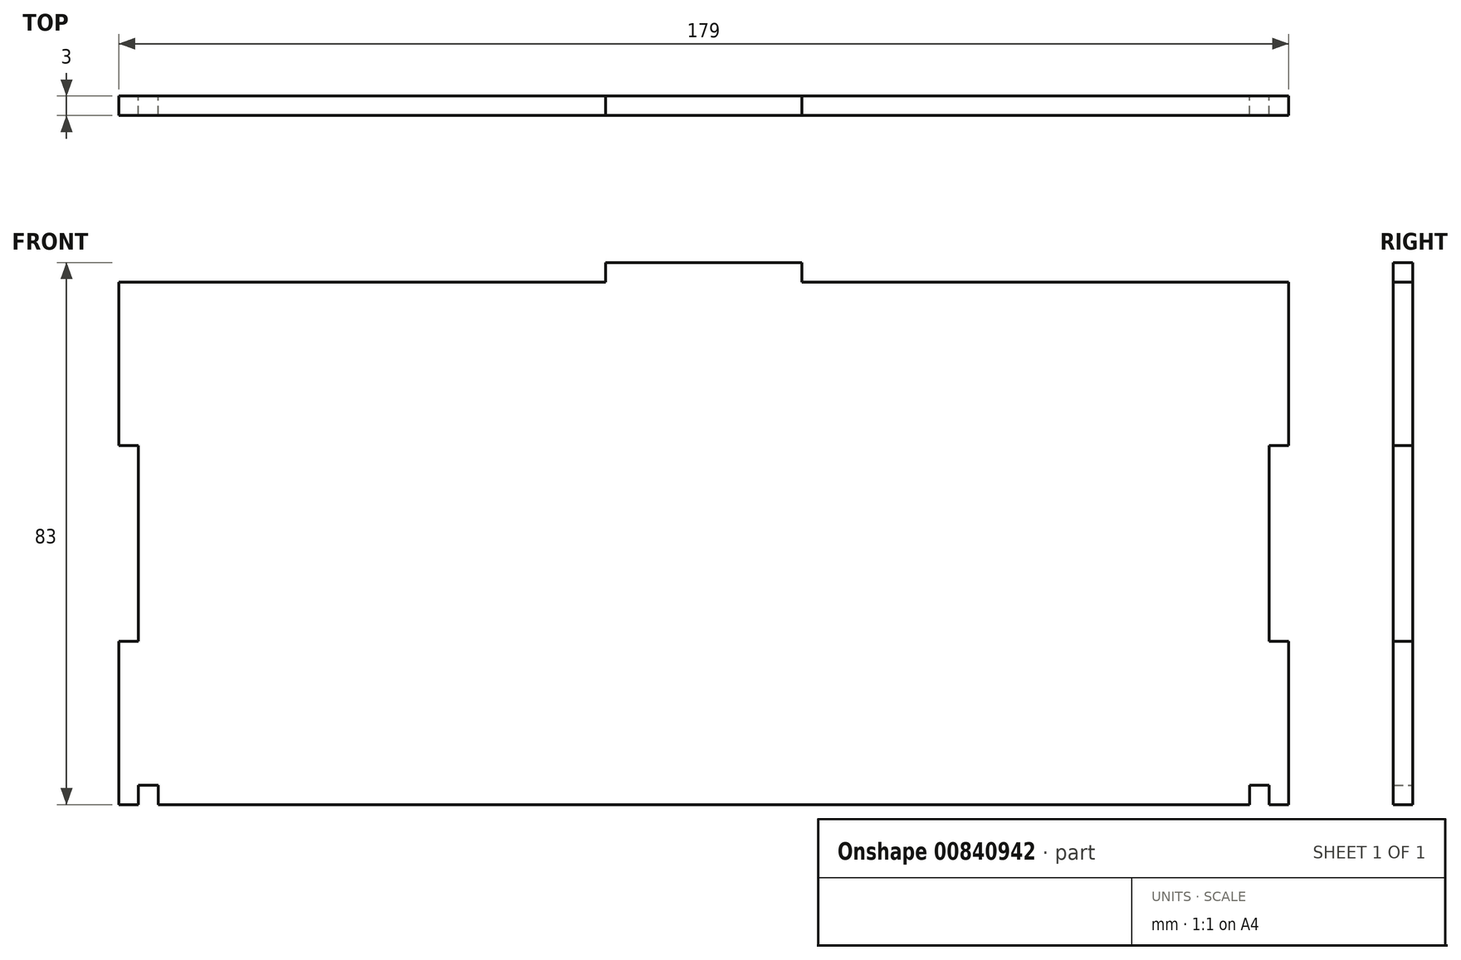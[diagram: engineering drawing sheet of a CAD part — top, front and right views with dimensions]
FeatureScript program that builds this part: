
annotation { "Feature Type Name" : "Feature", "Feature Type Description" : "" }
export const myFeature = defineFeature(function(context is Context, id is Id, definition is map)
    precondition{}
    {
        {
            var Q0;
            Q0=qCreatedBy(makeId("Front.planeOp"),FACE);
            var sketch = newSketch(context, id + "F0", { "sketchPlane" : qUnion([Q0])});
            skLineSegment(sketch, "E0.bottom", {"start": v(-83.25, 1.34) * mm, "end": v(95.75, 1.34) * mm});
            skLineSegment(sketch, "E0.top", {"start": v(-83.25, -78.66) * mm, "end": v(-80.25, -78.66) * mm});
            skLineSegment(sketch, "E0.left", {"start": v(-83.25, 1.34) * mm, "end": v(-83.25, -78.66) * mm});
            skLineSegment(sketch, "E0.right", {"start": v(95.75, 1.34) * mm, "end": v(95.75, -78.66) * mm});
            skLineSegment(sketch, "E1.top", {"start": v(-80.25, -75.66) * mm, "end": v(-77.25, -75.66) * mm});
            skLineSegment(sketch, "E1.left", {"start": v(-80.25, -78.66) * mm, "end": v(-80.25, -75.66) * mm});
            skLineSegment(sketch, "E1.right", {"start": v(-77.25, -78.66) * mm, "end": v(-77.25, -75.66) * mm});
            skLineSegment(sketch, "E2", {"start": v(6.25, 1.34) * mm, "end": v(6.25, -25.5) * mm, "construction": true});
            skLineSegment(sketch, "E3.trimOffspring", {"start": v(-77.25, -78.66) * mm, "end": v(89.75, -78.66) * mm});
            skLineSegment(sketch, "E4.MirrorCS", {"start": v(92.75, -78.66) * mm, "end": v(92.75, -75.66) * mm});
            skLineSegment(sketch, "E5.MirrorCS", {"start": v(92.75, -75.66) * mm, "end": v(89.75, -75.66) * mm});
            skLineSegment(sketch, "E6.MirrorCS", {"start": v(89.75, -78.66) * mm, "end": v(89.75, -75.66) * mm});
            skLineSegment(sketch, "E7.trimOffspring", {"start": v(92.75, -78.66) * mm, "end": v(95.75, -78.66) * mm});
            skLineSegment(sketch, "E8.bottom", {"start": v(-8.75, 4.34) * mm, "end": v(21.25, 4.34) * mm});
            skLineSegment(sketch, "E8.top", {"start": v(-8.75, 1.34) * mm, "end": v(21.25, 1.34) * mm});
            skLineSegment(sketch, "E8.left", {"start": v(-8.75, 4.34) * mm, "end": v(-8.75, 1.34) * mm});
            skLineSegment(sketch, "E8.right", {"start": v(21.25, 4.34) * mm, "end": v(21.25, 1.34) * mm});
            skSolve(sketch);
        }
        {
            var Q0;
            Q0 = qSketchRegion(id + "F0", true);
            extrude(context, id + "F1", {"entities" : qUnion([Q0]), "depth" : 3 * mm, "offsetDistance" : 25 * mm});
        }
        {
            var Q0;
            Q0=makeQuery(id+"F1.opExtrude","CAP_FACE",FACE,{"disambiguationData":[OSD([sQuery(id+"F0.wireOp",EDGE,"E0.bottom"),sQuery(id+"F0.wireOp",EDGE,"E0.top"),sQuery(id+"F0.wireOp",EDGE,"E0.left"),sQuery(id+"F0.wireOp",EDGE,"E0.right"),sQuery(id+"F0.wireOp",EDGE,"E1.top"),sQuery(id+"F0.wireOp",EDGE,"E1.left"),sQuery(id+"F0.wireOp",EDGE,"E1.right"),sQuery(id+"F0.wireOp",EDGE,"E3.trimOffspring"),sQuery(id+"F0.wireOp",EDGE,"E4.MirrorCS"),sQuery(id+"F0.wireOp",EDGE,"E5.MirrorCS"),sQuery(id+"F0.wireOp",EDGE,"E6.MirrorCS"),sQuery(id+"F0.wireOp",EDGE,"E7.trimOffspring")])],"isStart":false});
            var sketch = newSketch(context, id + "F2", { "sketchPlane" : qUnion([Q0])});
            skLineSegment(sketch, "E9.bottom", {"start": v(-83.25, -23.66) * mm, "end": v(-80.25, -23.66) * mm});
            skLineSegment(sketch, "E9.top", {"start": v(-83.25, -53.66) * mm, "end": v(-80.25, -53.66) * mm});
            skLineSegment(sketch, "E9.left", {"start": v(-83.25, -23.66) * mm, "end": v(-83.25, -53.66) * mm});
            skLineSegment(sketch, "E9.right", {"start": v(-80.25, -23.66) * mm, "end": v(-80.25, -53.66) * mm});
            skLineSegment(sketch, "E10", {"start": v(6.25, 4.34) * mm, "end": v(6.25, -35.76) * mm, "construction": true});
            skLineSegment(sketch, "E11.MirrorCS", {"start": v(95.75, -53.66) * mm, "end": v(92.75, -53.66) * mm});
            skLineSegment(sketch, "E12.MirrorCS", {"start": v(95.75, -23.66) * mm, "end": v(92.75, -23.66) * mm});
            skLineSegment(sketch, "E13.MirrorCS", {"start": v(92.75, -23.66) * mm, "end": v(92.75, -53.66) * mm});
            skLineSegment(sketch, "E14.MirrorCS", {"start": v(95.75, -23.66) * mm, "end": v(95.75, -53.66) * mm});
            skSolve(sketch);
        }
        {
            var Q0;
            Q0 = qSketchRegion(id + "F2", true);
            extrude(context, id + "F3", {"entities" : qUnion([Q0]), "operationType" : NewBodyOperationType.REMOVE, "oppositeDirection" : true, "depth" : 25 * mm, "offsetDistance" : 25 * mm});
        }
    });
